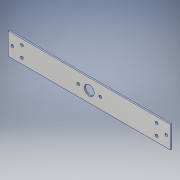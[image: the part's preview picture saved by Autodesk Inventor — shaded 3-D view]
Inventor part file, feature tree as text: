
AUTODESK INVENTOR PART (.ipt)
format: ipt  version: 2017 (Build 210142000, 142)  size: 126,976 bytes
history: native  units: in
note: dims shown in document units (in); Inventor stores cm internally (conversion verified against a paired STEP export)
features: hole x2, sketch x2, extrude x1
ambient origin geometry x8: Origin, YZ Plane, XZ Plane, XY Plane, X Axis, Y Axis, Z Axis, Center Point
bodies: Body1 (feature_tree)
feature tree (5):
  extrude  "Extrusion2"  Depth=14.75in
  hole  "Hole1"  [1 undecoded]
  hole  "Hole2"  [1 undecoded]
  sketch  "Sketch3"  dims[d0=14.75in d3=0.5in]
  sketch  "Sketch4"  dims[d4=1.0in d5=0.25in d6=0.25in d10=0.25in d11=1.25in d12=0.125in d13=0.0in d14=0.9in d15=0.75in d16=0.375in d17=0.25in d18=0.5635in d19=1.0in d20=0.8108in d21=1.0in d22=0.25in d23=0.25in d24=0.75in d25=0.375in d26=0.25in d27=0.5635in d28=1.0in d29=0.8108in]
note: 2 required parameter values undecoded (feature->parameter linkage not recoverable at this tier; creation-order binding heuristic only, values carry confidence <= 0.55)
